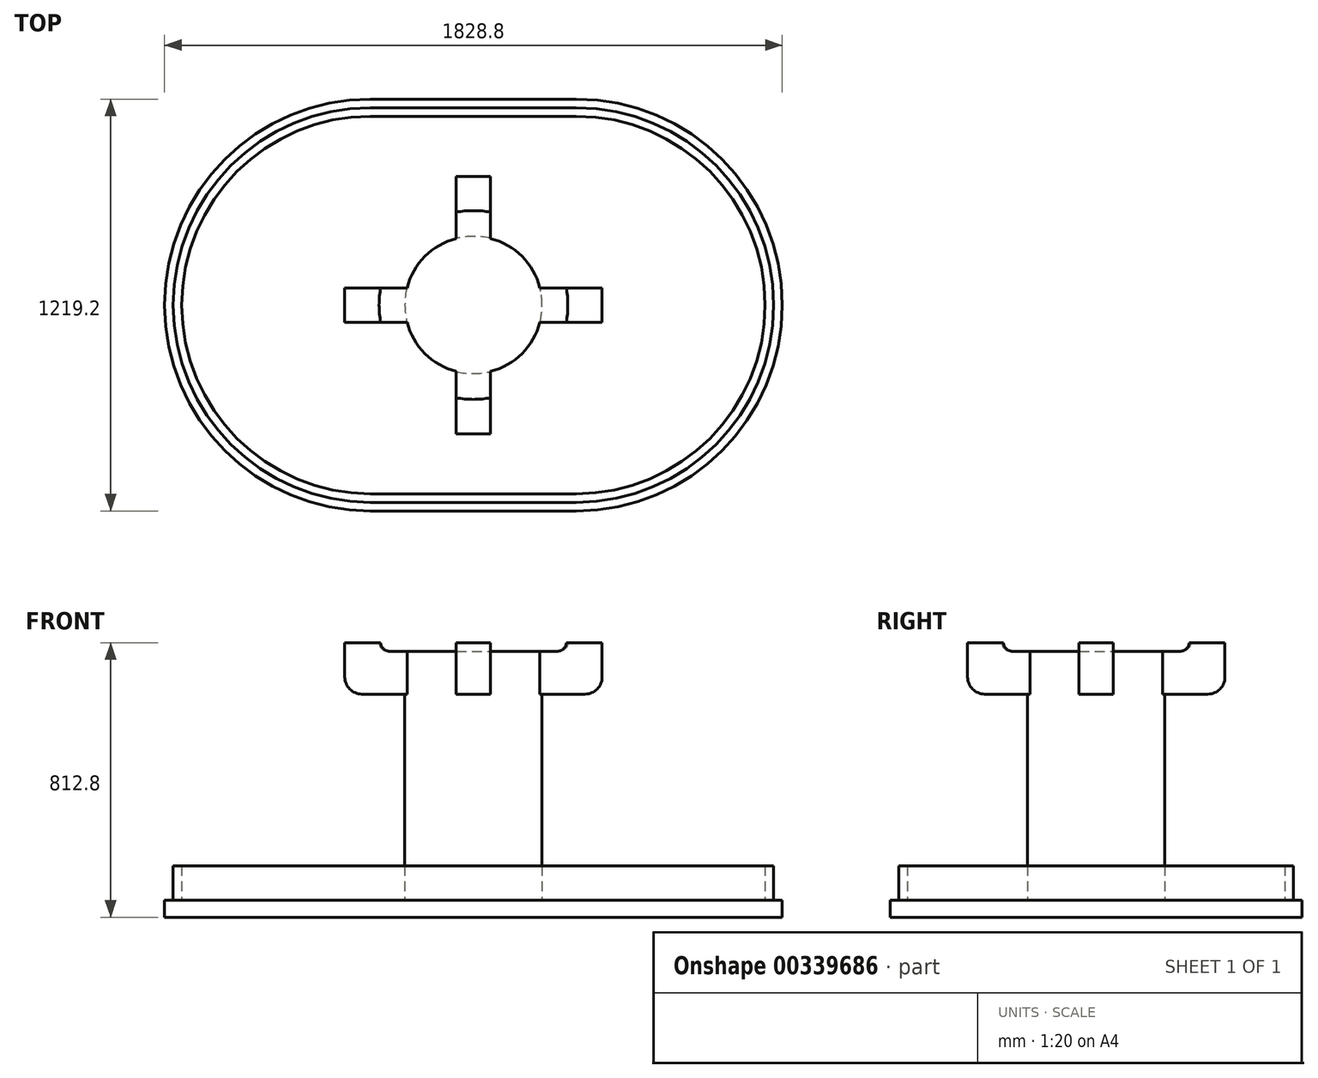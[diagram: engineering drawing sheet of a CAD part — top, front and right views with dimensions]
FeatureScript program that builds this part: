
annotation { "Feature Type Name" : "Feature", "Feature Type Description" : "" }
export const myFeature = defineFeature(function(context is Context, id is Id, definition is map)
    precondition{}
    {
        {
            var Q0;
            Q0=qCreatedBy(makeId("Top.planeOp"),FACE);
            var sketch = newSketch(context, id + "F0", { "sketchPlane" : qUnion([Q0])});
            skLineSegment(sketch, "E0.bottom", {"start": v(-304.8, 609.6) * mm, "end": v(304.8, 609.6) * mm});
            skLineSegment(sketch, "E0.top", {"start": v(-304.8, -609.6) * mm, "end": v(304.8, -609.6) * mm});
            skLineSegment(sketch, "E0.left", {"start": v(-304.8, 609.6) * mm, "end": v(-304.8, -609.6) * mm});
            skLineSegment(sketch, "E0.right", {"start": v(304.8, 609.6) * mm, "end": v(304.8, -609.6) * mm});
            skPoint(sketch, "E0.middle", {"position": v(0, 0) * mm});
            skArc(sketch, "E1", {"start": v(-304.8, 609.6) * mm, "mid": v(-914.4, 0) * mm, "end": v(-304.8, -609.6) * mm});
            skArc(sketch, "E2", {"start": v(304.8, -609.6) * mm, "mid": v(914.4, 0) * mm, "end": v(304.8, 609.6) * mm});
            skLineSegment(sketch, "E3.0", {"start": v(-304.8, -584.2) * mm, "end": v(304.8, -584.2) * mm});
            skArc(sketch, "E4.0", {"start": v(304.8, -584.2) * mm, "mid": v(889, 0) * mm, "end": v(304.8, 584.2) * mm});
            skLineSegment(sketch, "E5.0", {"start": v(-304.8, 584.2) * mm, "end": v(304.8, 584.2) * mm});
            skArc(sketch, "E5.1", {"start": v(-304.8, 584.2) * mm, "mid": v(-889, 0) * mm, "end": v(-304.8, -584.2) * mm});
            skLineSegment(sketch, "E6.0", {"start": v(-304.8, -558.8) * mm, "end": v(304.8, -558.8) * mm});
            skArc(sketch, "E6.1", {"start": v(-304.8, 558.8) * mm, "mid": v(-863.6, 0) * mm, "end": v(-304.8, -558.8) * mm});
            skLineSegment(sketch, "E6.2", {"start": v(-304.8, 558.8) * mm, "end": v(304.8, 558.8) * mm});
            skArc(sketch, "E6.3", {"start": v(304.8, -558.8) * mm, "mid": v(863.6, 0) * mm, "end": v(304.8, 558.8) * mm});
            skCircle(sketch, "E7", {"center": v(0, 0) * mm, "radius": 203.2 * mm});
            skSolve(sketch);
        }
        {
            var Q0;
            Q0=makeQuery(id+"F0.imprint","IMPRINT",FACE,{"disambiguationData":[TD([[makeQuery(id+"F0.imprint","IMPRINT",EDGE,{"derivedFrom":sQuery(id+"F0.wireOp",EDGE,"E0.left")}),-1.0]])]});
            var Q1;
            Q1=makeQuery(id+"F0.imprint","IMPRINT",FACE,{"disambiguationData":[TD([[makeQuery(id+"F0.imprint","IMPRINT",EDGE,{"derivedFrom":sQuery(id+"F0.wireOp",EDGE,"E0.bottom")}),-1.0]])]});
            var Q2;
            Q2=makeQuery(id+"F0.imprint","IMPRINT",FACE,{"disambiguationData":[TD([[makeQuery(id+"F0.imprint","IMPRINT",EDGE,{"derivedFrom":sQuery(id+"F0.wireOp",EDGE,"E0.right")}),1.0]])]});
            var Q3;
            {var subQ0=sQuery(id+"F0.wireOp",EDGE,"E0.top");Q3=makeQuery(id+"F0.imprint","IMPRINT",FACE,{"disambiguationData":[TD([[makeQuery(id+"F0.imprint","IMPRINT",EDGE,{"derivedFrom":subQ0}),1.0]])]});}
            var Q4;
            {var subQ0=sQuery(id+"F0.wireOp",EDGE,"E3.0");Q4=makeQuery(id+"F0.imprint","IMPRINT",FACE,{"disambiguationData":[TD([[makeQuery(id+"F0.imprint","IMPRINT",EDGE,{"derivedFrom":subQ0}),1.0]])]});}
            var Q5;
            {var subQ1=sQuery(id+"F0.wireOp",EDGE,"E6.0");Q5=makeQuery(id+"F0.imprint","IMPRINT",FACE,{"disambiguationData":[TD([[makeQuery(id+"F0.imprint","IMPRINT",EDGE,{"derivedFrom":subQ1}),1.0]])]});}
            var Q6;
            {var subQ0=sQuery(id+"F0.wireOp",EDGE,"E6.3");Q6=makeQuery(id+"F0.imprint","IMPRINT",FACE,{"disambiguationData":[TD([[makeQuery(id+"F0.imprint","IMPRINT",EDGE,{"derivedFrom":subQ0}),1.0]])]});}
            var Q7;
            {var subQ0=sQuery(id+"F0.wireOp",EDGE,"E6.1");Q7=makeQuery(id+"F0.imprint","IMPRINT",FACE,{"disambiguationData":[TD([[makeQuery(id+"F0.imprint","IMPRINT",EDGE,{"derivedFrom":subQ0}),1.0]])]});}
            var Q8;
            {var subQ0=sQuery(id+"F0.wireOp",EDGE,"E5.0");Q8=makeQuery(id+"F0.imprint","IMPRINT",FACE,{"disambiguationData":[TD([[makeQuery(id+"F0.imprint","IMPRINT",EDGE,{"derivedFrom":subQ0}),-1.0]])]});}
            var Q9;
            Q9=makeQuery(id+"F0.imprint","IMPRINT",FACE,{"disambiguationData":[TD([[makeQuery(id+"F0.imprint","IMPRINT",EDGE,{"derivedFrom":sQuery(id+"F0.wireOp",EDGE,"E7")}),1.0]])]});
            extrude(context, id + "F1", {"entities" : qUnion([Q0, Q1, Q2, Q3, Q4, Q5, Q6, Q7, Q8, Q9]), "oppositeDirection" : true, "depth" : 50.8 * mm});
        }
        {
            var Q0;
            {var subQ0=sQuery(id+"F0.wireOp",EDGE,"E5.1");Q0=makeQuery(id+"F0.imprint","IMPRINT",FACE,{"disambiguationData":[TD([[makeQuery(id+"F0.imprint","IMPRINT",EDGE,{"derivedFrom":subQ0}),1.0]])]});}
            var Q1;
            {var subQ0=sQuery(id+"F0.wireOp",EDGE,"E3.0");Q1=makeQuery(id+"F0.imprint","IMPRINT",FACE,{"disambiguationData":[TD([[makeQuery(id+"F0.imprint","IMPRINT",EDGE,{"derivedFrom":subQ0}),1.0]])]});}
            var Q2;
            {var subQ0=sQuery(id+"F0.wireOp",EDGE,"E5.0");Q2=makeQuery(id+"F0.imprint","IMPRINT",FACE,{"disambiguationData":[TD([[makeQuery(id+"F0.imprint","IMPRINT",EDGE,{"derivedFrom":subQ0}),-1.0]])]});}
            var Q3;
            {var subQ0=sQuery(id+"F0.wireOp",EDGE,"E4.0");Q3=makeQuery(id+"F0.imprint","IMPRINT",FACE,{"disambiguationData":[TD([[makeQuery(id+"F0.imprint","IMPRINT",EDGE,{"derivedFrom":subQ0}),1.0]])]});}
            extrude(context, id + "F2", {"entities" : qUnion([Q0, Q1, Q2, Q3]), "operationType" : NewBodyOperationType.ADD, "depth" : 101.6 * mm});
        }
        {
            var Q0;
            Q0=makeQuery(id+"F0.imprint","IMPRINT",FACE,{"disambiguationData":[TD([[makeQuery(id+"F0.imprint","IMPRINT",EDGE,{"derivedFrom":sQuery(id+"F0.wireOp",EDGE,"E7")}),1.0]])]});
            extrude(context, id + "F3", {"entities" : qUnion([Q0]), "operationType" : NewBodyOperationType.ADD, "depth" : 762 * mm});
        }
        {
            var Q0;
            Q0=qCreatedBy(makeId("Front.planeOp"),FACE);
            var sketch = newSketch(context, id + "F4", { "sketchPlane" : qUnion([Q0])});
            skLineSegment(sketch, "E8.bottom", {"start": v(50.8, 609.6) * mm, "end": v(-50.8, 609.6) * mm});
            skLineSegment(sketch, "E8.top", {"start": v(50.8, 762) * mm, "end": v(-50.8, 762) * mm});
            skLineSegment(sketch, "E8.left", {"start": v(50.8, 609.6) * mm, "end": v(50.8, 762) * mm});
            skLineSegment(sketch, "E8.right", {"start": v(-50.8, 609.6) * mm, "end": v(-50.8, 762) * mm});
            skPoint(sketch, "E8.middle", {"position": v(0, 685.8) * mm});
            skSolve(sketch);
        }
        {
            var Q0;
            Q0 = qSketchRegion(id + "F4", true);
            extrude(context, id + "F5", {"entities" : qUnion([Q0]), "operationType" : NewBodyOperationType.ADD, "endBound" : BoundingType.SYMMETRIC, "oppositeDirection" : true, "depth" : 762 * mm});
        }
        {
            var Q0;
            Q0=qCreatedBy(makeId("Right.planeOp"),FACE);
            var sketch = newSketch(context, id + "F6", { "sketchPlane" : qUnion([Q0])});
            skLineSegment(sketch, "E9.bottom", {"start": v(50.8, 609.6) * mm, "end": v(-50.8, 609.6) * mm});
            skLineSegment(sketch, "E9.top", {"start": v(50.8, 762) * mm, "end": v(-50.8, 762) * mm});
            skLineSegment(sketch, "E9.left", {"start": v(50.8, 609.6) * mm, "end": v(50.8, 762) * mm});
            skLineSegment(sketch, "E9.right", {"start": v(-50.8, 609.6) * mm, "end": v(-50.8, 762) * mm});
            skPoint(sketch, "E9.middle", {"position": v(0, 685.8) * mm});
            skSolve(sketch);
        }
        {
            var Q0;
            Q0 = qSketchRegion(id + "F6", true);
            extrude(context, id + "F7", {"entities" : qUnion([Q0]), "operationType" : NewBodyOperationType.ADD, "endBound" : BoundingType.SYMMETRIC, "depth" : 762 * mm});
        }
        {
            var Q0;
            Q0=makeQuery(id+"F5.opExtrude","CAP_EDGE",EDGE,{"disambiguationData":[OSD([sQuery(id+"F4.wireOp",EDGE,"E8.bottom")])],"isStart":true});
            var Q1;
            Q1=makeQuery(id+"F7.opExtrude","CAP_EDGE",EDGE,{"disambiguationData":[OSD([sQuery(id+"F6.wireOp",EDGE,"E9.bottom")])],"isStart":true});
            var Q2;
            Q2=makeQuery(id+"F5.opExtrude","CAP_EDGE",EDGE,{"disambiguationData":[OSD([sQuery(id+"F4.wireOp",EDGE,"E8.bottom")])],"isStart":false});
            var Q3;
            Q3=makeQuery(id+"F7.opExtrude","CAP_EDGE",EDGE,{"disambiguationData":[OSD([sQuery(id+"F6.wireOp",EDGE,"E9.bottom")])],"isStart":false});
            fillet(context, id + "F8", {"entities" : qUnion([Q0, Q1, Q2, Q3]), "radius" : 50.8 * mm, "tangentPropagation" : true, "allowEdgeOverflow" : false});
        }
        {
            var Q0;
            Q0=makeQuery(id+"F7.boolean.opBoolean","MERGE",FACE,{"derivedFrom":[makeQuery(id+"F5.boolean.opBoolean","MERGE",FACE,{"derivedFrom":[makeQuery(id+"F3.opExtrude","CAP_FACE",FACE,{"disambiguationData":[OSD([sQuery(id+"F0.wireOp",EDGE,"E7")])],"isStart":false}),makeQuery(id+"F5.opExtrude","SWEPT_FACE",FACE,{"disambiguationData":[OSD([sQuery(id+"F4.wireOp",EDGE,"E8.top")])]})]}),makeQuery(id+"F7.opExtrude","SWEPT_FACE",FACE,{"disambiguationData":[OSD([sQuery(id+"F6.wireOp",EDGE,"E9.top")])]})]});
            var sketch = newSketch(context, id + "F9", { "sketchPlane" : qUnion([Q0])});
            skCircle(sketch, "E10", {"center": v(0, 0) * mm, "radius": 279.4 * mm});
            skSolve(sketch);
        }
        {
            var Q0;
            Q0 = qSketchRegion(id + "F9", true);
            extrude(context, id + "F10", {"entities" : qUnion([Q0]), "operationType" : NewBodyOperationType.REMOVE, "oppositeDirection" : true, "depth" : 25.4 * mm});
        }
        {
            var Q0;
            {var subQ0=sQuery(id+"F9.wireOp",EDGE,"E10");Q0=makeQuery(id+"F10.boolean.opBoolean","COPY",EDGE,{"disambiguationData":[TD([makeQuery(id+"F7.opExtrude","SWEPT_FACE",FACE,{"disambiguationData":[OSD([sQuery(id+"F6.wireOp",EDGE,"E9.left")])]}),makeQuery(id+"F7.opExtrude","SWEPT_FACE",FACE,{"disambiguationData":[OSD([sQuery(id+"F6.wireOp",EDGE,"E9.right")])]}),makeQuery(id+"F10.opExtrude","SWEPT_FACE",FACE,{"disambiguationData":[OSD([subQ0])]}),makeQuery(id+"F10.opExtrude","CAP_FACE",FACE,{"disambiguationData":[OSD([subQ0])],"isStart":false})]),OD(0.0)],"derivedFrom":makeQuery(id+"F10.opExtrude","CAP_EDGE",EDGE,{"disambiguationData":[OSD([subQ0])],"isStart":false})});}
            var Q1;
            {var subQ0=sQuery(id+"F9.wireOp",EDGE,"E10");Q1=makeQuery(id+"F10.boolean.opBoolean","COPY",EDGE,{"disambiguationData":[TD([makeQuery(id+"F5.opExtrude","SWEPT_FACE",FACE,{"disambiguationData":[OSD([sQuery(id+"F4.wireOp",EDGE,"E8.left")])]}),makeQuery(id+"F5.opExtrude","SWEPT_FACE",FACE,{"disambiguationData":[OSD([sQuery(id+"F4.wireOp",EDGE,"E8.right")])]}),makeQuery(id+"F10.opExtrude","SWEPT_FACE",FACE,{"disambiguationData":[OSD([subQ0])]}),makeQuery(id+"F10.opExtrude","CAP_FACE",FACE,{"disambiguationData":[OSD([subQ0])],"isStart":false})]),OD(1.0)],"derivedFrom":makeQuery(id+"F10.opExtrude","CAP_EDGE",EDGE,{"disambiguationData":[OSD([subQ0])],"isStart":false})});}
            var Q2;
            {var subQ0=sQuery(id+"F9.wireOp",EDGE,"E10");Q2=makeQuery(id+"F10.boolean.opBoolean","COPY",EDGE,{"disambiguationData":[TD([makeQuery(id+"F7.opExtrude","SWEPT_FACE",FACE,{"disambiguationData":[OSD([sQuery(id+"F6.wireOp",EDGE,"E9.left")])]}),makeQuery(id+"F7.opExtrude","SWEPT_FACE",FACE,{"disambiguationData":[OSD([sQuery(id+"F6.wireOp",EDGE,"E9.right")])]}),makeQuery(id+"F10.opExtrude","SWEPT_FACE",FACE,{"disambiguationData":[OSD([subQ0])]}),makeQuery(id+"F10.opExtrude","CAP_FACE",FACE,{"disambiguationData":[OSD([subQ0])],"isStart":false})]),OD(1.0)],"derivedFrom":makeQuery(id+"F10.opExtrude","CAP_EDGE",EDGE,{"disambiguationData":[OSD([subQ0])],"isStart":false})});}
            var Q3;
            {var subQ0=sQuery(id+"F9.wireOp",EDGE,"E10");Q3=makeQuery(id+"F10.boolean.opBoolean","COPY",EDGE,{"disambiguationData":[TD([makeQuery(id+"F5.opExtrude","SWEPT_FACE",FACE,{"disambiguationData":[OSD([sQuery(id+"F4.wireOp",EDGE,"E8.left")])]}),makeQuery(id+"F5.opExtrude","SWEPT_FACE",FACE,{"disambiguationData":[OSD([sQuery(id+"F4.wireOp",EDGE,"E8.right")])]}),makeQuery(id+"F10.opExtrude","SWEPT_FACE",FACE,{"disambiguationData":[OSD([subQ0])]}),makeQuery(id+"F10.opExtrude","CAP_FACE",FACE,{"disambiguationData":[OSD([subQ0])],"isStart":false})]),OD(0.0)],"derivedFrom":makeQuery(id+"F10.opExtrude","CAP_EDGE",EDGE,{"disambiguationData":[OSD([subQ0])],"isStart":false})});}
            fillet(context, id + "F11", {"entities" : qUnion([Q0, Q1, Q2, Q3]), "radius" : 25.4 * mm, "tangentPropagation" : true, "allowEdgeOverflow" : false});
        }
    });
